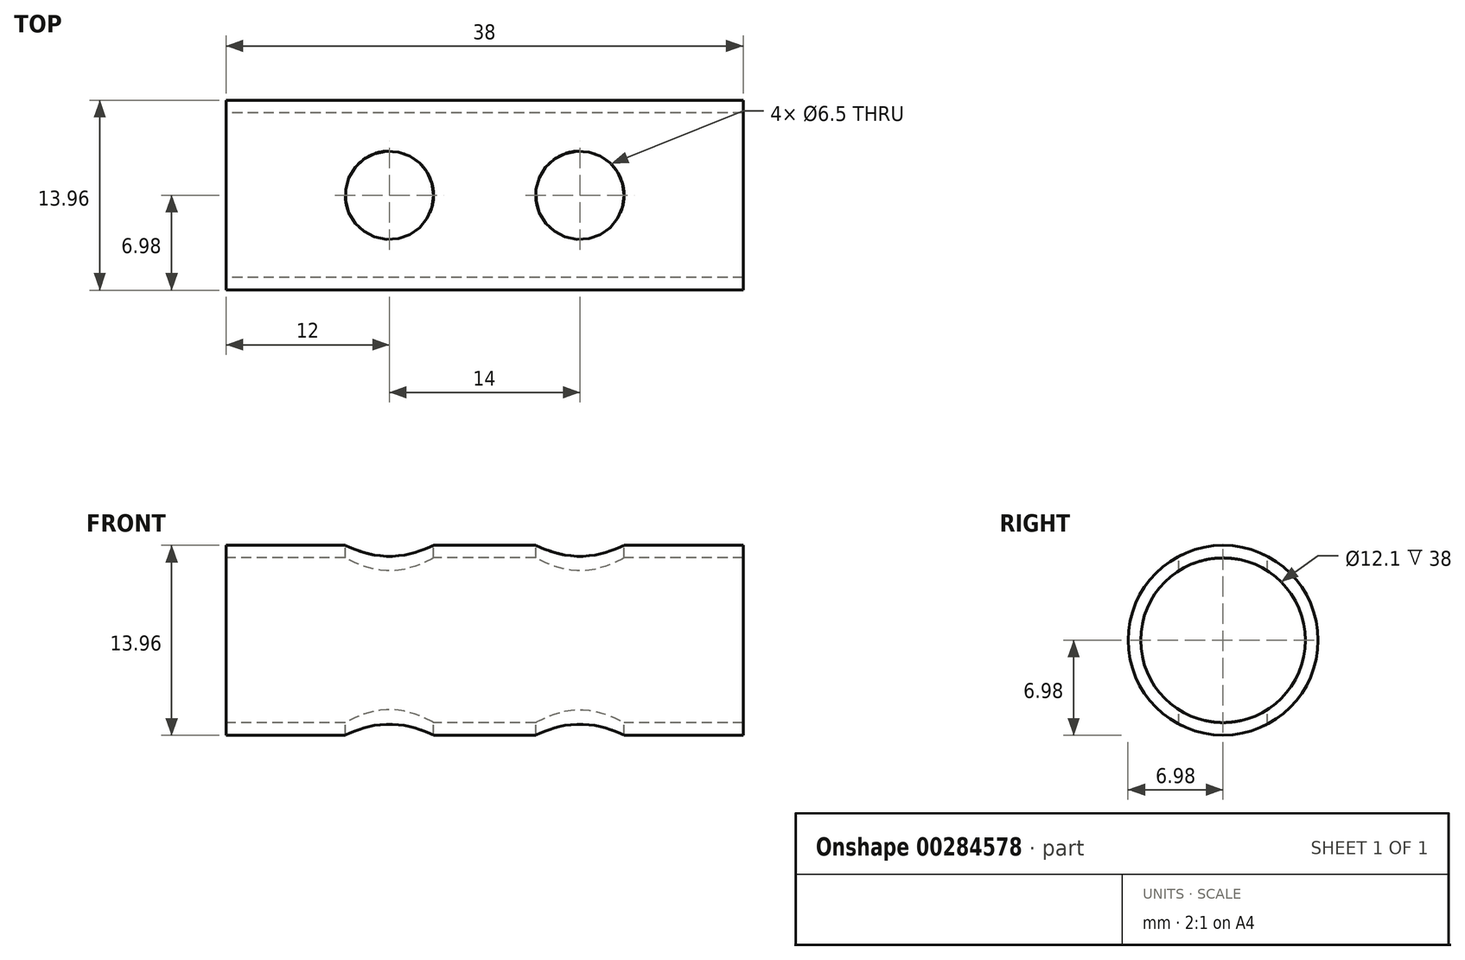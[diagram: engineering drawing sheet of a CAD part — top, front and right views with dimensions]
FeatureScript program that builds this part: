
annotation { "Feature Type Name" : "Feature", "Feature Type Description" : "" }
export const myFeature = defineFeature(function(context is Context, id is Id, definition is map)
    precondition{}
    {
        {
            var Q0;
            Q0=qCreatedBy(makeId("Right.planeOp"),FACE);
            var sketch = newSketch(context, id + "F0", { "sketchPlane" : qUnion([Q0])});
            skCircle(sketch, "E0", {"center": v(0, 0) * mm, "radius": 6.97 * mm});
            skCircle(sketch, "E1", {"center": v(0, 0) * mm, "radius": 6.05 * mm});
            skSolve(sketch);
        }
        {
            var Q0;
            Q0=qSketchRegion(id+"F0",true);
            extrude(context, id + "F1", {"entities" : qUnion([Q0]), "depth" : 38 * mm});
        }
        {
            var Q0;
            Q0=qCreatedBy(makeId("Top.planeOp"),FACE);
            cPlane(context, id + "F2", {"entities" : qUnion([Q0]), "cplaneType" : CPlaneType.OFFSET, "offset" : 7 * mm, "width" : 150 * mm, "height" : 150 * mm});
        }
        {
            var Q0;
            Q0=qCreatedBy(id+"F2.planeOp",FACE);
            var sketch = newSketch(context, id + "F3", { "sketchPlane" : qUnion([Q0])});
            skPoint(sketch, "E2", {"position": v(12, 0) * mm});
            skCircle(sketch, "E3", {"center": v(12, 0) * mm, "radius": 3.25 * mm});
            skPoint(sketch, "E4", {"position": v(26, 0) * mm});
            skCircle(sketch, "E5", {"center": v(26, 0) * mm, "radius": 3.25 * mm});
            skSolve(sketch);
        }
        {
            var Q0;
            Q0=qSketchRegion(id+"F3",true);
            extrude(context, id + "F4", {"entities" : qUnion([Q0]), "operationType" : NewBodyOperationType.REMOVE, "oppositeDirection" : true, "depth" : 14 * mm});
        }
    });
